# Revit family: VZT jednotka
name_source: partatom
category: Mechanické zařízení
revit_build: Autodesk Revit 2018 (Build: 20170223_1515(x64)
units: mm (PartAtom-declared; Revit-internal decimal feet)

## family parameters
Bod výpočtu místnosti = Ne
Kóta kulaté spojky = Použít průměr
Nadpis OmniClass = Climate Control (HVAC)
Ořezat dutým tvarem při načtení = Ne
Sdílené = Ne
Typ dílu = Normální
Vždy vertikální = Ano
Založené na pracovní rovině = Ne
Číslo OmniClass = 23.75.00.00

## types (1)
- VZT jednotka
    DÉLKA = 3900 mm
    Konektor 1_Výška = 500 mm  [stored 1.64042 ft]
    Konektor 1_Šířka = 500 mm  [stored 1.64042 ft]
    Konektor 2_Výška = 500 mm  [stored 1.64042 ft]
    Konektor 2_Šířka = 500 mm  [stored 1.64042 ft]
    Konektor 3_Výška = 500 mm  [stored 1.64042 ft]
    Konektor 3_Šířka = 500 mm  [stored 1.64042 ft]
    Konektor 4_Výška = 500 mm  [stored 1.64042 ft]
    Konektor 4_Šířka = 500 mm  [stored 1.64042 ft]
    Konektor 5_Výška = 1 mm  [stored 0.00328084 ft]
    Konektor 5_Šířka = 1 mm  [stored 0.00328084 ft]
    Popis = VZT jednotka
    URL = www.cadconsulting.cz
    VÝŠKA = 2000 mm  [stored 6.56168 ft]
    ŠÍŘKA = 800 mm  [stored 2.62467 ft]

note: [stored X ft] marks values corroborated as IEEE doubles in the binary element streams (Revit-internal decimal feet)
